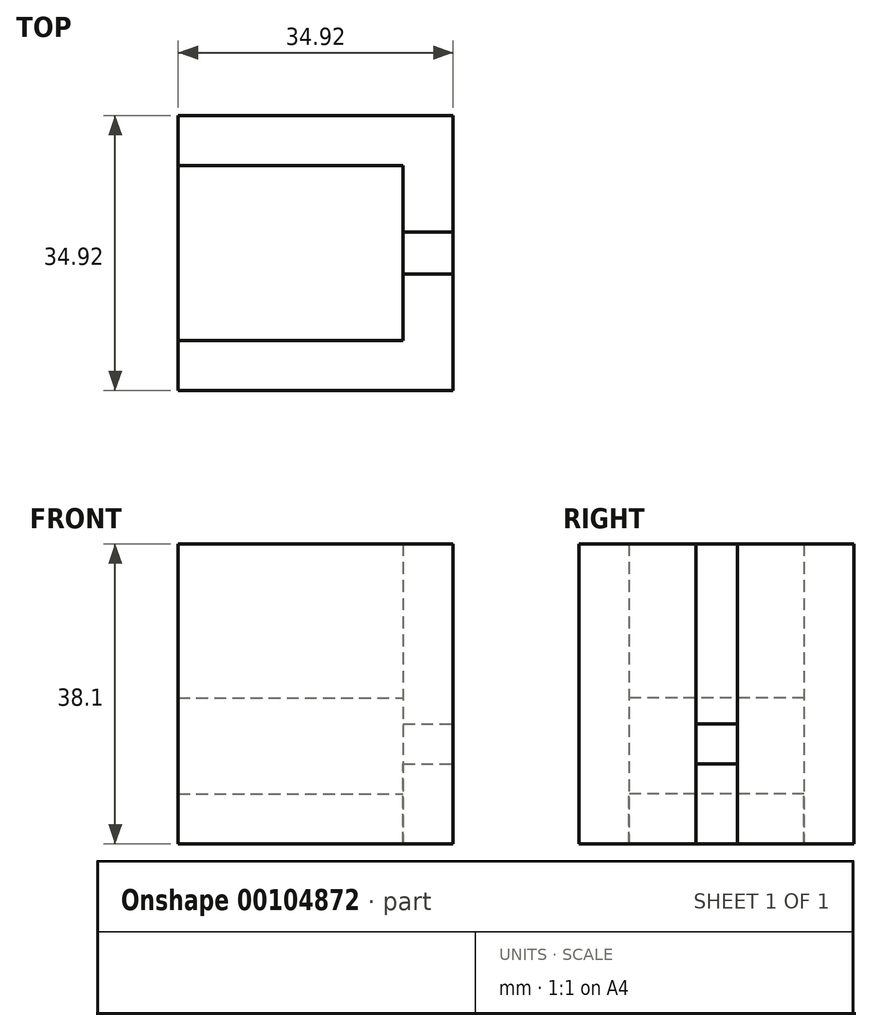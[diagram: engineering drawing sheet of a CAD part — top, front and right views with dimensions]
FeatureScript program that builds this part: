
annotation { "Feature Type Name" : "Feature", "Feature Type Description" : "" }
export const myFeature = defineFeature(function(context is Context, id is Id, definition is map)
    precondition{}
    {
        {
            var Q0;
            Q0=qCreatedBy(makeId("Top.planeOp"),FACE);
            var sketch = newSketch(context, id + "F0", { "sketchPlane" : qUnion([Q0])});
            skLineSegment(sketch, "E0.bottom", {"start": v(-17.46, 17.46) * mm, "end": v(17.46, 17.46) * mm});
            skLineSegment(sketch, "E0.top", {"start": v(-17.46, -17.46) * mm, "end": v(17.46, -17.46) * mm});
            skLineSegment(sketch, "E0.left", {"start": v(-17.46, 17.46) * mm, "end": v(-17.46, -17.46) * mm});
            skLineSegment(sketch, "E0.right", {"start": v(17.46, 17.46) * mm, "end": v(17.46, -17.46) * mm});
            skPoint(sketch, "E0.middle", {"position": v(0, 0) * mm});
            skPoint(sketch, "E1", {"position": v(-17.46, 11.11) * mm});
            skPoint(sketch, "E2", {"position": v(-17.46, -11.11) * mm});
            skPoint(sketch, "E3", {"position": v(11.11, 17.46) * mm});
            skLineSegment(sketch, "E4", {"start": v(-17.46, 11.11) * mm, "end": v(11.11, 11.11) * mm});
            skLineSegment(sketch, "E5", {"start": v(11.11, 11.11) * mm, "end": v(11.11, 2.65) * mm});
            skLineSegment(sketch, "E6", {"start": v(11.11, -11.11) * mm, "end": v(-17.46, -11.11) * mm});
            skPoint(sketch, "E7", {"position": v(11.11, 2.65) * mm});
            skPoint(sketch, "E8", {"position": v(11.11, -2.65) * mm});
            skLineSegment(sketch, "E9", {"start": v(11.11, 2.65) * mm, "end": v(17.46, 2.65) * mm});
            skLineSegment(sketch, "E10", {"start": v(11.11, -2.65) * mm, "end": v(17.46, -2.65) * mm});
            skLineSegment(sketch, "E11.trimOffspring", {"start": v(11.11, -2.65) * mm, "end": v(11.11, -11.11) * mm});
            skLineSegment(sketch, "E12", {"start": v(11.11, 2.65) * mm, "end": v(11.11, -2.65) * mm});
            skSolve(sketch);
        }
        {
            var Q0;
            {var subQ0=sQuery(id+"F0.wireOp",EDGE,"E4");Q0=makeQuery(id+"F0.imprint","IMPRINT",FACE,{"disambiguationData":[TD([[makeQuery(id+"F0.imprint","IMPRINT",EDGE,{"derivedFrom":subQ0}),-1.0]])]});}
            extrude(context, id + "F1", {"entities" : qUnion([Q0]), "depth" : 31.75 * mm, "hasSecondDirection" : true, "secondDirectionOppositeDirection" : false, "secondDirectionDepth" : 12.2 * mm});
        }
        {
            var Q0;
            {var subQ0=sQuery(id+"F0.wireOp",EDGE,"E4");Q0=makeQuery(id+"F0.imprint","IMPRINT",FACE,{"disambiguationData":[TD([[makeQuery(id+"F0.imprint","IMPRINT",EDGE,{"derivedFrom":subQ0}),-1.0]])]});}
            extrude(context, id + "F2", {"entities" : qUnion([Q0]), "oppositeDirection" : true, "depth" : 6.35 * mm});
        }
        {
            var Q0;
            {var subQ2=sQuery(id+"F0.wireOp",EDGE,"E0.bottom");Q0=makeQuery(id+"F0.imprint","IMPRINT",FACE,{"disambiguationData":[TD([[makeQuery(id+"F0.imprint","IMPRINT",EDGE,{"derivedFrom":subQ2}),-1.0]])]});}
            var Q1;
            {var subQ2=sQuery(id+"F0.wireOp",EDGE,"E0.top");Q1=makeQuery(id+"F0.imprint","IMPRINT",FACE,{"disambiguationData":[TD([[makeQuery(id+"F0.imprint","IMPRINT",EDGE,{"derivedFrom":subQ2}),1.0]])]});}
            extrude(context, id + "F3", {"entities" : qUnion([Q0, Q1]), "depth" : 31.75 * mm, "hasSecondDirection" : true, "secondDirectionOppositeDirection" : true, "secondDirectionDepth" : 6.35 * mm});
        }
        {
            var Q0;
            {var subQ0=sQuery(id+"F0.wireOp",EDGE,"E9");Q0=makeQuery(id+"F0.imprint","IMPRINT",FACE,{"disambiguationData":[TD([[makeQuery(id+"F0.imprint","IMPRINT",EDGE,{"derivedFrom":subQ0}),-1.0]])]});}
            extrude(context, id + "F4", {"entities" : qUnion([Q0]), "oppositeDirection" : true, "depth" : 6.35 * mm, "hasSecondDirection" : true, "secondDirectionOppositeDirection" : false, "secondDirectionDepth" : 3.8 * mm});
        }
        {
            var Q0;
            {var subQ0=sQuery(id+"F0.wireOp",EDGE,"E9");Q0=makeQuery(id+"F0.imprint","IMPRINT",FACE,{"disambiguationData":[TD([[makeQuery(id+"F0.imprint","IMPRINT",EDGE,{"derivedFrom":subQ0}),-1.0]])]});}
            extrude(context, id + "F5", {"entities" : qUnion([Q0]), "depth" : 31.75 * mm, "hasSecondDirection" : true, "secondDirectionOppositeDirection" : false, "secondDirectionDepth" : 8.9 * mm});
        }
    });
